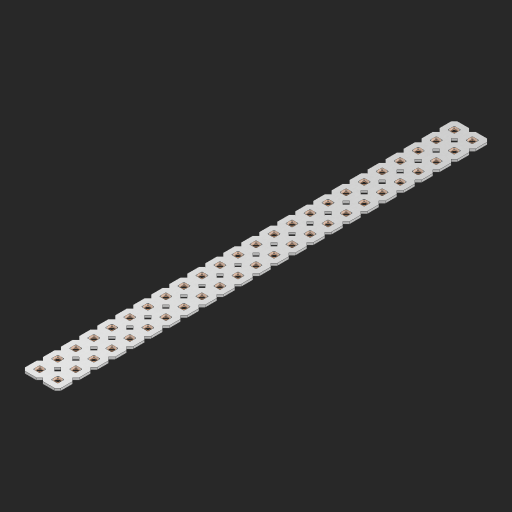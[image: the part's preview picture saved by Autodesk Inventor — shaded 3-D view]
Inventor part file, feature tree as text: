
AUTODESK INVENTOR PART (.ipt)
format: ipt  version: 2023 (Build 270158000, 158)  size: 827,392 bytes
history: native  units: in
note: dims shown in document units (in); Inventor stores cm internally (conversion verified against a paired STEP export)
features: other x49, extrude x47, sketch x2, pattern_linear x1
ambient origin geometry x8: Origin, YZ Plane, XZ Plane, XY Plane, X Axis, Y Axis, Z Axis, Center Point
bodies: Solid1 (feature_tree), Body (feature_tree)
feature tree (99):
  pattern_linear  "Rectangular Pattern1"  Spacing1=0.09in  [1 undecoded]
  sketch  "Sketch1"  dims[d1=0.5in]
  sketch  "Sketch2"  dims[d2=0.182in d3=0.09in d4=0.09in d5=0.09in d6=0.09in d7=0.09in d8=0.09in d9=0.09in d10=0.09in d11=0.02in d13=0.0in d14=0.172in d15=0.0625in d16=0.0in d19=0.5in d22=0.5in]
  other  "Srf1"
  other  "Srf126"
  other  "Srf127"
  other  "Srf128"
  other  "Srf129"
  other  "Srf130"
  other  "Srf131"
  other  "Srf250"
  other  "Srf251"
  other  "Srf252"
  other  "Srf253"
  other  "Srf254"
  other  "Srf255"
  other  "Srf256"
  other  "Srf257"
  other  "Srf258"
  other  "Srf259"
  other  "Srf260"
  other  "Srf261"
  other  "Srf262"
  other  "Srf263"
  other  "Srf264"
  other  "Srf265"
  other  "Srf266"
  other  "Srf268"
  other  "Srf269"
  other  "Srf270"
  other  "Srf271"
  other  "Srf272"
  other  "Srf273"
  other  "Srf274"
  other  "Srf275"
  other  "Srf276"
  other  "Srf277"
  other  "Srf278"
  other  "Srf279"
  other  "Srf280"
  other  "Srf281"
  other  "Srf282"
  other  "Srf283"
  other  "Srf284"
  other  "Srf285"
  other  "Srf286"
  other  "Srf287"
  other  "Srf288"
  other  "Srf289"
  other  "Srf290"
  other  "Srf291"
  other  "Circle"
  extrude  "ExtrusionSrf126"  Depth=0.09in
  extrude  "ExtrusionSrf127"  Depth=0.09in
  extrude  "ExtrusionSrf128"  Depth=0.09in
  extrude  "ExtrusionSrf129"  Depth=0.09in
  extrude  "ExtrusionSrf130"  Depth=0.09in
  extrude  "ExtrusionSrf131"  Depth=0.09in
  extrude  "ExtrusionSrf250"  Depth=0.09in
  extrude  "ExtrusionSrf251"  Depth=0.02in
  extrude  "ExtrusionSrf252"  TaperAngle=0.0deg  [1 undecoded]
  extrude  "ExtrusionSrf253"  Depth=0.5in
  extrude  "ExtrusionSrf254"  Depth=0.0625in TaperAngle=0.0deg
  extrude  "ExtrusionSrf255"  Depth=0.5in
  extrude  "ExtrusionSrf256"  Depth=0.5in
  extrude  "ExtrusionSrf257"  [1 undecoded]
  extrude  "ExtrusionSrf258"  [1 undecoded]
  extrude  "ExtrusionSrf259"  [1 undecoded]
  extrude  "ExtrusionSrf260"  [1 undecoded]
  extrude  "ExtrusionSrf261"  [1 undecoded]
  extrude  "ExtrusionSrf262"  [1 undecoded]
  extrude  "ExtrusionSrf263"  [1 undecoded]
  extrude  "ExtrusionSrf264"  [1 undecoded]
  extrude  "ExtrusionSrf265"  [1 undecoded]
  extrude  "ExtrusionSrf266"  [1 undecoded]
  extrude  "ExtrusionSrf268"  [1 undecoded]
  extrude  "ExtrusionSrf269"  [1 undecoded]
  extrude  "ExtrusionSrf270"  [1 undecoded]
  extrude  "ExtrusionSrf271"  [1 undecoded]
  extrude  "ExtrusionSrf272"  [1 undecoded]
  extrude  "ExtrusionSrf273"  [1 undecoded]
  extrude  "ExtrusionSrf274"  [1 undecoded]
  extrude  "ExtrusionSrf275"  [1 undecoded]
  extrude  "ExtrusionSrf276"  [1 undecoded]
  extrude  "ExtrusionSrf277"  [1 undecoded]
  extrude  "ExtrusionSrf278"  [1 undecoded]
  extrude  "ExtrusionSrf279"  [1 undecoded]
  extrude  "ExtrusionSrf280"  [1 undecoded]
  extrude  "ExtrusionSrf281"  [1 undecoded]
  extrude  "ExtrusionSrf282"  [1 undecoded]
  extrude  "ExtrusionSrf283"  [1 undecoded]
  extrude  "ExtrusionSrf284"  [1 undecoded]
  extrude  "ExtrusionSrf285"  [1 undecoded]
  extrude  "ExtrusionSrf286"  [1 undecoded]
  extrude  "ExtrusionSrf287"  [1 undecoded]
  extrude  "ExtrusionSrf288"  [1 undecoded]
  extrude  "ExtrusionSrf289"  [1 undecoded]
  extrude  "ExtrusionSrf290"  [1 undecoded]
  extrude  "ExtrusionSrf291"  [1 undecoded]
note: 36 required parameter values undecoded (feature->parameter linkage not recoverable at this tier; creation-order binding heuristic only, values carry confidence <= 0.55)
